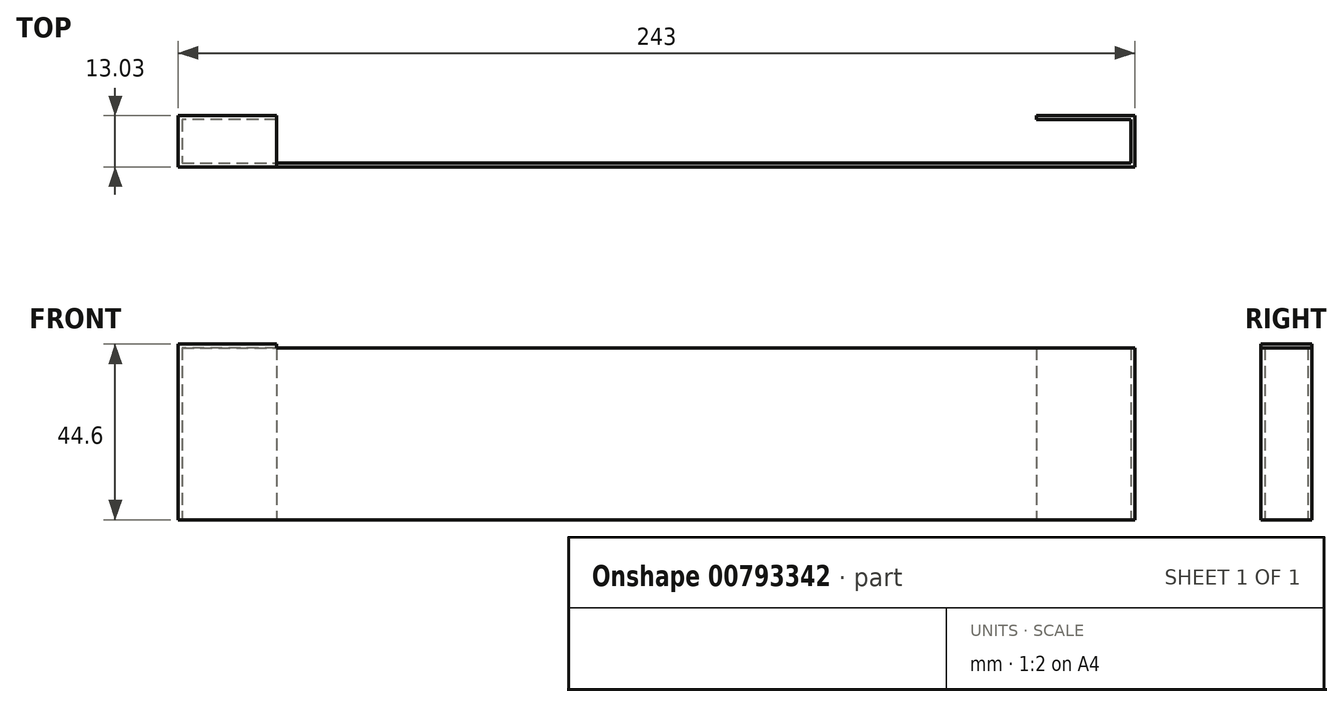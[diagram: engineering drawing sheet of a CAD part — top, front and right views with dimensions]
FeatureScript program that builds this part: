
annotation { "Feature Type Name" : "Feature", "Feature Type Description" : "" }
export const myFeature = defineFeature(function(context is Context, id is Id, definition is map)
    precondition{}
    {
        {
            var Q0;
            Q0=qCreatedBy(makeId("Top.planeOp"),FACE);
            var sketch = newSketch(context, id + "F0", { "sketchPlane" : qUnion([Q0])});
            skLineSegment(sketch, "E0", {"start": v(0, -65.8) * mm, "end": v(0, 59.73) * mm, "construction": true});
            skLineSegment(sketch, "E1", {"start": v(-96.5, 0) * mm, "end": v(-120.5, 0) * mm});
            skLineSegment(sketch, "E2", {"start": v(-120.5, 0) * mm, "end": v(-120.5, -11.03) * mm});
            skLineSegment(sketch, "E3", {"start": v(-120.5, -11.03) * mm, "end": v(120.5, -11.03) * mm});
            skLineSegment(sketch, "E4", {"start": v(120.5, -11.03) * mm, "end": v(120.5, 0) * mm});
            skLineSegment(sketch, "E5", {"start": v(120.5, 0) * mm, "end": v(96.5, 0) * mm});
            skLineSegment(sketch, "E6", {"start": v(96.5, 0) * mm, "end": v(96.5, 1) * mm});
            skLineSegment(sketch, "E7", {"start": v(96.5, 1) * mm, "end": v(121.5, 1) * mm});
            skLineSegment(sketch, "E8", {"start": v(121.5, 1) * mm, "end": v(121.5, -12.03) * mm});
            skLineSegment(sketch, "E9", {"start": v(121.5, -12.03) * mm, "end": v(-121.5, -12.03) * mm});
            skLineSegment(sketch, "E10", {"start": v(-121.5, -12.03) * mm, "end": v(-121.5, 1) * mm});
            skLineSegment(sketch, "E11", {"start": v(-121.5, 1) * mm, "end": v(-96.5, 1) * mm});
            skLineSegment(sketch, "E12", {"start": v(-96.5, 0) * mm, "end": v(-96.5, 1) * mm});
            skSolve(sketch);
        }
        {
            var Q0;
            Q0 = qSketchRegion(id + "F0", true);
            extrude(context, id + "F1", {"entities" : qUnion([Q0]), "depth" : 43.6 * mm, "offsetDistance" : 25 * mm});
        }
        {
            var Q0;
            Q0=makeQuery(id+"F1.opExtrude","CAP_FACE",FACE,{"disambiguationData":[OSD([sQuery(id+"F0.wireOp",EDGE,"E1"),sQuery(id+"F0.wireOp",EDGE,"E2"),sQuery(id+"F0.wireOp",EDGE,"E3"),sQuery(id+"F0.wireOp",EDGE,"E4"),sQuery(id+"F0.wireOp",EDGE,"E5"),sQuery(id+"F0.wireOp",EDGE,"E6"),sQuery(id+"F0.wireOp",EDGE,"E7"),sQuery(id+"F0.wireOp",EDGE,"E8"),sQuery(id+"F0.wireOp",EDGE,"E9"),sQuery(id+"F0.wireOp",EDGE,"E10"),sQuery(id+"F0.wireOp",EDGE,"E11"),sQuery(id+"F0.wireOp",EDGE,"E12")])],"isStart":false});
            var sketch = newSketch(context, id + "F2", { "sketchPlane" : qUnion([Q0])});
            skLineSegment(sketch, "E13.bottom", {"start": v(-96.5, 1) * mm, "end": v(-121.5, 1) * mm});
            skLineSegment(sketch, "E13.top", {"start": v(-96.5, -12.03) * mm, "end": v(-121.5, -12.03) * mm});
            skLineSegment(sketch, "E13.left", {"start": v(-96.5, 1) * mm, "end": v(-96.5, -12.03) * mm});
            skLineSegment(sketch, "E13.right", {"start": v(-121.5, 1) * mm, "end": v(-121.5, -12.03) * mm});
            skSolve(sketch);
        }
        {
            var Q0;
            Q0 = qSketchRegion(id + "F2", true);
            extrude(context, id + "F3", {"entities" : qUnion([Q0]), "operationType" : NewBodyOperationType.ADD, "depth" : 1 * mm, "offsetDistance" : 25 * mm});
        }
    });
